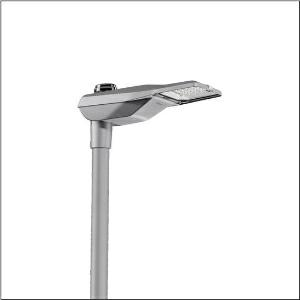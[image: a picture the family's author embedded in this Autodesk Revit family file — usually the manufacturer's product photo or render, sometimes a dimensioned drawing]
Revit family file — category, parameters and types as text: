
# Revit family: streetlight_sl_21_micro___pl52_5xe5h37n08db_9470
name_source: partatom
category: Lighting Fixtures
units: mm (PartAtom-declared; Revit-internal decimal feet)

## family parameters
Cut with Voids When Loaded = No
Host = Face
Light Source = No
Part Type = Normal
Room Calculation Point = No
Round Connector Dimension = Use Diameter
Shared = No

## types (1)
- --- (1 x LED, 5020 lm, 39.1 W, 3000K)
    Apparent Load = 39 VA
    CIE Flux Codes = 27 59 98 100 100
    Color Rendering = 70
    Color Temperature = 3000K
    Default Elevation = 1800 mm
    Description = Streetlight SL 21 micro, mast luminaire, primary light control with lens, of PMMA, primary optical cover: cover, of toughened safety glass, transparent, light distribution: PL52, light emission: direct distribution, primary light characteristic: asymmetric, installation type: post-top, LED, 3G 1.5mm², High Power LED, rated luminous flux: 5.020lm, luminous efficacy: 128lm/W, light colour: 730, colour temperature: 3000K, control: overheat protection, presetting dimming linear, constant luminous flux control, time-dependent luminous flux control, flexible luminous flux parameterisation, mains connection: 230..240V, AC, 50/60Hz, connection cable pre-assembled, cable length: 6,5m, wiring characteristics: H07RN-F, start of lifetime: 39W, end of service life: 41W, reduction: 18W, luminaire housing, of diecast aluminium (EN AC-44300), powder-coated, Siteco® metallic grey (DB 702S), corrosivity category C5 mid according to DIN EN ISO 12944, multi-level sealing system, sealing non-destructively replaceable, inclination adjustable: 0°, 5°, 10°, 15°, length: 528mm, width: 235mm, height: 110mm, spigot size: 76/60mm (post-top), protection rating (complete): IP66, insulation class (complete): insulation class I (protective earthing), certification: CE, ENEC, ENEC+, VDE, impact resistance: IK09, permissible operating ambient temperature for outdoor applications: -40..+50°C, standard-compliant lighting for roads and squares, packaging unit: 1 piece

Light Distribution: PL52
    Height = 110 mm
    Lamp = 1 x LED
    Lamp Light Flux = 5020 lm
    Lamp Power = 39.1 W
    Lamp count = 1
    Length = 528 mm
    Luminous efficacy = 128 lm/W
    Manufacturer = Siteco
    ModVariant = No
    Model = 5XE5H37N08DB
    Number of Poles = 1
    OnlyDefault = Yes
    Power Factor = 1
    Product Name = Streetlight SL 21 micro | PL52
    Product group = mast luminaire | pylon top
    ProductGroupID = 6100
    Protection Class = Protection class I
    Protection Degree = IP 66
    RLX_Detail_Level = 1
    RLX_Emergency_Light_Flux = 0 lm
    RLX_Emergency_Type = 0
    RLX_Emergency_Type_DB = No
    RlxData = <blob elided: 107829 chars, md5=17311365>
    Socket = socket
    Standby Power = 0 W
    System Light Flux = 5020 lm
    System Power = 39 W
    Type Comments = factory setting: luminous flux: 100 % | dim-lin: 254 | 765 mA
    Type Image = l_1294375.jpg
    URL = http://relux.com
    VarID = @adj_086569
    Voltage = 0 V
    Weight = 0.00 kg
    Width = 235 mm

## geometry (parser evidence)
native form markers: Blend x4, Sweep x11
no freeform markers — native parametric forms only
